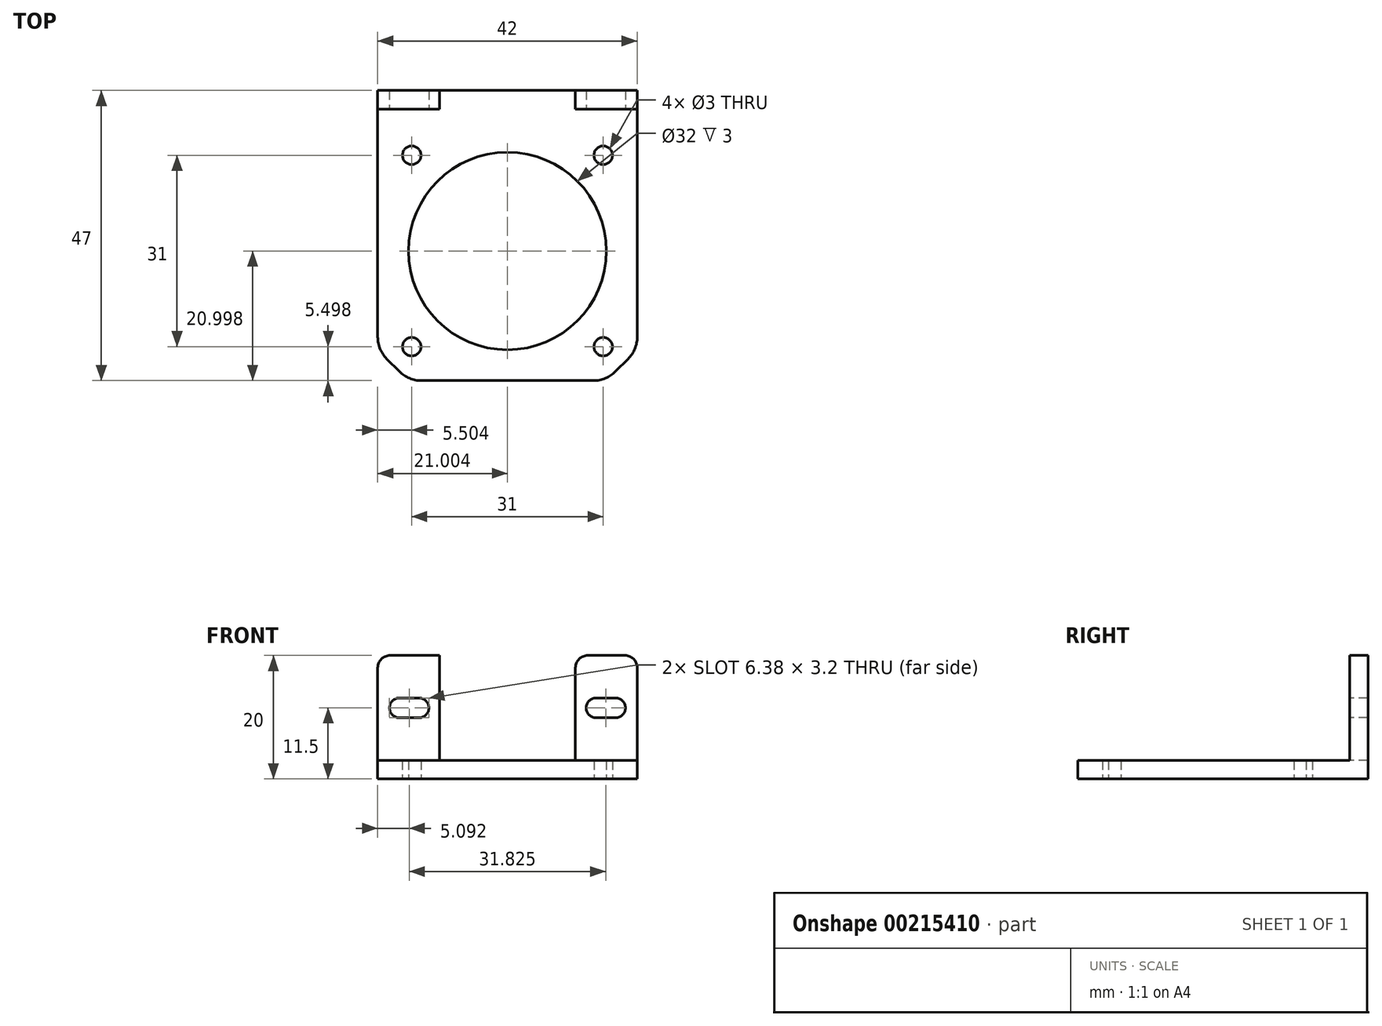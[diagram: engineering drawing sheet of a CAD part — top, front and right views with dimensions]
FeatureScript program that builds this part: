
annotation { "Feature Type Name" : "Feature", "Feature Type Description" : "" }
export const myFeature = defineFeature(function(context is Context, id is Id, definition is map)
    precondition{}
    {
        {
            var Q0;
            Q0=qCreatedBy(makeId("Top.planeOp"),FACE);
            var sketch = newSketch(context, id + "F0", { "sketchPlane" : qUnion([Q0])});
            skLineSegment(sketch, "E0.0.0", {"start": v(-91.98, -79.77) * mm, "end": v(-91.98, -47.77) * mm});
            skLineSegment(sketch, "E0.0.4", {"start": v(-133.98, -47.77) * mm, "end": v(-133.98, -79.77) * mm});
            skLineSegment(sketch, "E0.0.5", {"start": v(-133.98, -79.77) * mm, "end": v(-128.98, -84.77) * mm});
            skLineSegment(sketch, "E0.0.6", {"start": v(-128.98, -84.77) * mm, "end": v(-96.98, -84.77) * mm});
            skLineSegment(sketch, "E0.0.7", {"start": v(-96.98, -84.77) * mm, "end": v(-91.98, -79.77) * mm});
            skCircle(sketch, "E1.0", {"center": v(-97.48, -79.27) * mm, "radius": 1.5 * mm});
            skCircle(sketch, "E1.1", {"center": v(-97.48, -48.27) * mm, "radius": 1.5 * mm});
            skCircle(sketch, "E1.2", {"center": v(-128.48, -48.27) * mm, "radius": 1.5 * mm});
            skCircle(sketch, "E1.3", {"center": v(-128.48, -79.27) * mm, "radius": 1.5 * mm});
            skCircle(sketch, "E2.0", {"center": v(-112.98, -63.77) * mm, "radius": 16 * mm});
            skLineSegment(sketch, "E3", {"start": v(-133.98, -42.77) * mm, "end": v(-133.98, -47.77) * mm});
            skLineSegment(sketch, "E4", {"start": v(-91.98, -42.77) * mm, "end": v(-91.98, -47.77) * mm});
            skLineSegment(sketch, "E5", {"start": v(-133.98, -42.77) * mm, "end": v(-133.98, -37.77) * mm});
            skLineSegment(sketch, "E6", {"start": v(-133.98, -37.77) * mm, "end": v(-91.98, -37.77) * mm});
            skLineSegment(sketch, "E7", {"start": v(-91.98, -37.77) * mm, "end": v(-91.98, -42.77) * mm});
            skLineSegment(sketch, "E8", {"start": v(-91.98, -40.77) * mm, "end": v(-133.98, -40.77) * mm});
            skPoint(sketch, "E8.endSnap0", {"position": v(-133.98, -40.27) * mm});
            skCircle(sketch, "E9.1", {"center": v(-36.1, -52.13) * mm, "radius": 1.5 * mm});
            skCircle(sketch, "E9.2", {"center": v(-67.1, -52.13) * mm, "radius": 1.5 * mm});
            skLineSegment(sketch, "E10", {"start": v(-67.1, -52.13) * mm, "end": v(-36.1, -52.13) * mm, "construction": true});
            skLineSegment(sketch, "E11.bottom", {"start": v(-30.6, -56.13) * mm, "end": v(-72.6, -56.13) * mm});
            skLineSegment(sketch, "E11.top", {"start": v(-30.6, -48.13) * mm, "end": v(-72.6, -48.13) * mm});
            skLineSegment(sketch, "E11.left", {"start": v(-30.6, -56.13) * mm, "end": v(-30.6, -48.13) * mm});
            skLineSegment(sketch, "E11.right", {"start": v(-72.6, -56.13) * mm, "end": v(-72.6, -48.13) * mm});
            skPoint(sketch, "E11.middle", {"position": v(-51.6, -52.13) * mm});
            skSolve(sketch);
        }
        {
            var Q0;
            Q0=makeQuery(id+"F0.imprint","IMPRINT",FACE,{"disambiguationData":[TD([[makeQuery(id+"F0.imprint","IMPRINT",EDGE,{"derivedFrom":sQuery(id+"F0.wireOp",EDGE,"E0.0.0")}),1.0]])]});
            extrude(context, id + "F1", {"entities" : qUnion([Q0]), "depth" : 3 * mm});
        }
        {
            var Q0;
            {var subQ0=sQuery(id+"F0.wireOp",EDGE,"E6");Q0=makeQuery(id+"F0.imprint","IMPRINT",FACE,{"disambiguationData":[TD([[makeQuery(id+"F0.imprint","IMPRINT",EDGE,{"derivedFrom":subQ0}),-1.0]])]});}
            extrude(context, id + "F2", {"entities" : qUnion([Q0]), "operationType" : NewBodyOperationType.ADD, "depth" : 20 * mm});
        }
        {
            var Q0;
            Q0=makeQuery(id+"F2.opExtrude","SWEPT_FACE",FACE,{"disambiguationData":[OSD([sQuery(id+"F0.wireOp",EDGE,"E8")])]});
            var sketch = newSketch(context, id + "F3", { "sketchPlane" : qUnion([Q0])});
            skLineSegment(sketch, "E12", {"start": v(-95.48, 3) * mm, "end": v(-95.48, 20) * mm, "construction": true});
            skLineSegment(sketch, "E13", {"start": v(-101.98, 20) * mm, "end": v(-101.98, 3) * mm});
            skLineSegment(sketch, "E14", {"start": v(-112.98, 3) * mm, "end": v(-112.98, 20) * mm, "construction": true});
            skLineSegment(sketch, "E15", {"start": v(-95.48, 11.5) * mm, "end": v(-98.65, 11.5) * mm, "construction": true});
            skArc(sketch, "E16.0.startCap", {"start": v(-95.48, 13.1) * mm, "mid": v(-93.88, 11.5) * mm, "end": v(-95.48, 9.9) * mm});
            skArc(sketch, "E16.0.endCap", {"start": v(-98.65, 9.9) * mm, "mid": v(-100.25, 11.5) * mm, "end": v(-98.65, 13.1) * mm});
            skLineSegment(sketch, "E16.0.left", {"start": v(-95.48, 9.9) * mm, "end": v(-98.65, 9.9) * mm});
            skLineSegment(sketch, "E16.0.right", {"start": v(-95.48, 13.1) * mm, "end": v(-98.65, 13.1) * mm});
            skLineSegment(sketch, "E17.MirrorCS", {"start": v(-130.48, 13.1) * mm, "end": v(-127.3, 13.1) * mm});
            skLineSegment(sketch, "E18.MirrorCS", {"start": v(-130.48, 9.9) * mm, "end": v(-127.3, 9.9) * mm});
            skArc(sketch, "E19.MirrorCS", {"start": v(-127.3, 9.9) * mm, "mid": v(-125.7, 11.5) * mm, "end": v(-127.3, 13.1) * mm});
            skArc(sketch, "E20.MirrorCS", {"start": v(-130.48, 13.1) * mm, "mid": v(-132.08, 11.5) * mm, "end": v(-130.48, 9.9) * mm});
            skLineSegment(sketch, "E21", {"start": v(-123.98, 3) * mm, "end": v(-123.98, 20) * mm});
            skSolve(sketch);
        }
        {
            var Q0;
            Q0=qSketchRegion(id+"F3",true);
            extrude(context, id + "F4", {"entities" : qUnion([Q0]), "operationType" : NewBodyOperationType.REMOVE, "oppositeDirection" : true, "depth" : 25 * mm});
        }
        {
            var Q0;
            {var subQ0=sQuery(id+"F3.wireOp",EDGE,"E13");Q0=makeQuery(id+"F3.imprint","IMPRINT",FACE,{"disambiguationData":[TD([[makeQuery(id+"F3.imprint","IMPRINT",EDGE,{"derivedFrom":subQ0}),-1.0]])]});}
            extrude(context, id + "F5", {"entities" : qUnion([Q0]), "operationType" : NewBodyOperationType.REMOVE, "oppositeDirection" : true, "depth" : 25 * mm});
        }
        {
            var Q0;
            {var subQ0=sQuery(id+"F0.wireOp",EDGE,"E7");var subQ3=sQuery(id+"F0.wireOp",EDGE,"E8");var subQ5=makeQuery(id+"F1.opExtrude","CAP_EDGE",EDGE,{"disambiguationData":[OSD([subQ3])],"isStart":false});Q0=makeQuery(id+"F5.boolean.opBoolean","SPLIT",EDGE,{"disambiguationData":[TD([makeQuery(id+"F2.opExtrude","SWEPT_FACE",FACE,{"disambiguationData":[OSD([subQ0])]})])],"derivedFrom":subQ5});}
            var Q1;
            {var subQ0=sQuery(id+"F0.wireOp",EDGE,"E5");var subQ3=sQuery(id+"F0.wireOp",EDGE,"E8");var subQ5=makeQuery(id+"F1.opExtrude","CAP_EDGE",EDGE,{"disambiguationData":[OSD([subQ3])],"isStart":false});Q1=makeQuery(id+"F5.boolean.opBoolean","SPLIT",EDGE,{"disambiguationData":[TD([makeQuery(id+"F2.opExtrude","SWEPT_FACE",FACE,{"disambiguationData":[OSD([subQ0])]})])],"derivedFrom":subQ5});}
            var Q2;
            Q2=makeQuery(id+"F2.opExtrude","CAP_EDGE",EDGE,{"disambiguationData":[OSD([sQuery(id+"F0.wireOp",EDGE,"E7")])],"isStart":false});
            var Q3;
            {var subQ0=sQuery(id+"F3.wireOp",EDGE,"E13");var subQ1=sQuery(id+"F0.wireOp",EDGE,"E8");Q3=makeQuery(id+"F5.boolean.opBoolean","COPY",EDGE,{"derivedFrom":makeQuery(id+"F5.opExtrude","SWEPT_EDGE",EDGE,{"disambiguationData":[OSD([subQ1,subQ0]),TDD([makeQuery(id+"F3.imprint","INTERSECT",VERTEX,{"derivedFrom":[makeQuery(id+"F2.opExtrude","CAP_EDGE",EDGE,{"disambiguationData":[OSD([subQ1])],"isStart":false}),subQ0]})])]})});}
            var Q4;
            {var subQ0=sQuery(id+"F3.wireOp",EDGE,"E21");var subQ1=sQuery(id+"F0.wireOp",EDGE,"E8");Q4=makeQuery(id+"F5.boolean.opBoolean","COPY",EDGE,{"derivedFrom":makeQuery(id+"F5.opExtrude","SWEPT_EDGE",EDGE,{"disambiguationData":[OSD([subQ1,subQ0]),TDD([makeQuery(id+"F3.imprint","INTERSECT",VERTEX,{"derivedFrom":[makeQuery(id+"F2.opExtrude","CAP_EDGE",EDGE,{"disambiguationData":[OSD([subQ1])],"isStart":false}),subQ0]})])]})});}
            var Q5;
            Q5=makeQuery(id+"F2.opExtrude","CAP_EDGE",EDGE,{"disambiguationData":[OSD([sQuery(id+"F0.wireOp",EDGE,"E5")])],"isStart":false});
            fillet(context, id + "F6", {"entities" : qUnion([Q0, Q1, Q2, Q3, Q4, Q5]), "radius" : 2 * mm, "tangentPropagation" : true, "allowEdgeOverflow" : false});
        }
        {
            var Q0;
            Q0=makeQuery(id+"F1.opExtrude","SWEPT_EDGE",EDGE,{"disambiguationData":[OSD([sQuery(id+"F0.wireOp",EDGE,"E0.0.4"),sQuery(id+"F0.wireOp",EDGE,"E0.0.5")])]});
            var Q1;
            Q1=makeQuery(id+"F1.opExtrude","SWEPT_EDGE",EDGE,{"disambiguationData":[OSD([sQuery(id+"F0.wireOp",EDGE,"E0.0.5"),sQuery(id+"F0.wireOp",EDGE,"E0.0.6")])]});
            var Q2;
            Q2=makeQuery(id+"F1.opExtrude","SWEPT_EDGE",EDGE,{"disambiguationData":[OSD([sQuery(id+"F0.wireOp",EDGE,"E0.0.6"),sQuery(id+"F0.wireOp",EDGE,"E0.0.7")])]});
            var Q3;
            Q3=makeQuery(id+"F1.opExtrude","SWEPT_EDGE",EDGE,{"disambiguationData":[OSD([sQuery(id+"F0.wireOp",EDGE,"E0.0.0"),sQuery(id+"F0.wireOp",EDGE,"E0.0.7")])]});
            fillet(context, id + "F7", {"entities" : qUnion([Q0, Q1, Q2, Q3]), "radius" : 5 * mm, "tangentPropagation" : true, "allowEdgeOverflow" : false});
        }
    });
